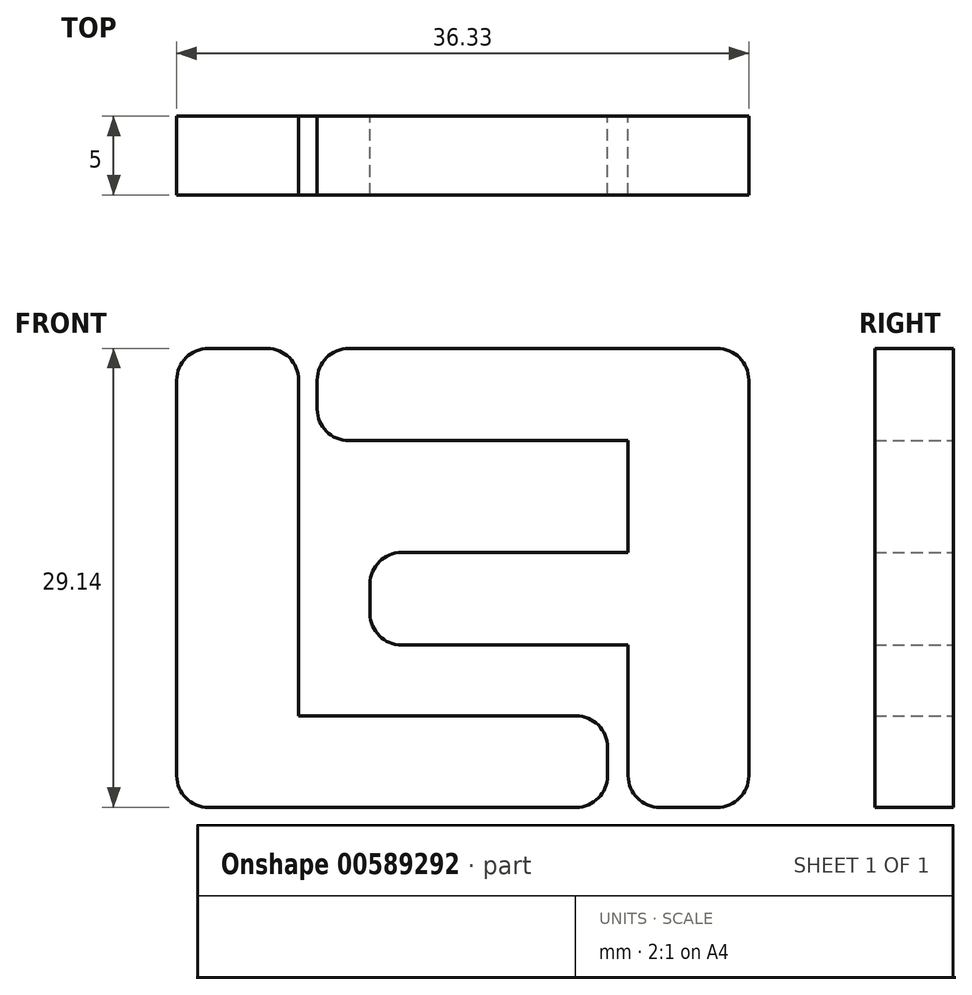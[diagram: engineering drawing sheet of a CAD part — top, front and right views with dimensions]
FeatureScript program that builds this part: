
annotation { "Feature Type Name" : "Feature", "Feature Type Description" : "" }
export const myFeature = defineFeature(function(context is Context, id is Id, definition is map)
    precondition{}
    {
        {
            var Q0;
            Q0=qCreatedBy(makeId("Front.planeOp"),FACE);
            var sketch = newSketch(context, id + "F0", { "sketchPlane" : qUnion([Q0])});
            skLineSegment(sketch, "E0", {"start": v(-17.2, 14.75) * mm, "end": v(-17.2, -14.4) * mm});
            skLineSegment(sketch, "E1", {"start": v(-17.2, -14.4) * mm, "end": v(10.15, -14.4) * mm});
            skLineSegment(sketch, "E2", {"start": v(10.15, -14.4) * mm, "end": v(10.15, -8.6) * mm});
            skLineSegment(sketch, "E3", {"start": v(10.15, -8.6) * mm, "end": v(-9.47, -8.6) * mm});
            skLineSegment(sketch, "E4", {"start": v(-9.47, -8.6) * mm, "end": v(-9.47, 14.75) * mm});
            skLineSegment(sketch, "E5", {"start": v(-9.47, 14.75) * mm, "end": v(-17.2, 14.75) * mm});
            skLineSegment(sketch, "E6", {"start": v(-8.29, 14.75) * mm, "end": v(-8.29, 8.9) * mm});
            skLineSegment(sketch, "E7", {"start": v(-8.29, 8.9) * mm, "end": v(11.46, 8.9) * mm});
            skLineSegment(sketch, "E8", {"start": v(11.46, 8.9) * mm, "end": v(11.46, 1.8) * mm});
            skLineSegment(sketch, "E9", {"start": v(11.46, 1.8) * mm, "end": v(-4.93, 1.8) * mm});
            skLineSegment(sketch, "E10", {"start": v(-4.93, 1.8) * mm, "end": v(-4.93, -4.09) * mm});
            skLineSegment(sketch, "E11", {"start": v(-4.93, -4.09) * mm, "end": v(11.46, -4.09) * mm});
            skLineSegment(sketch, "E12", {"start": v(11.46, -4.09) * mm, "end": v(11.46, -14.4) * mm});
            skLineSegment(sketch, "E13", {"start": v(11.46, -14.4) * mm, "end": v(19.12, -14.4) * mm});
            skLineSegment(sketch, "E14", {"start": v(19.12, -14.4) * mm, "end": v(19.12, 14.75) * mm});
            skLineSegment(sketch, "E15", {"start": v(19.12, 14.75) * mm, "end": v(-8.29, 14.75) * mm});
            skSolve(sketch);
        }
        {
            var Q0;
            Q0 = qSketchRegion(id + "F0", true);
            extrude(context, id + "F1", {"entities" : qUnion([Q0]), "depth" : 5 * mm, "offsetDistance" : 25 * mm});
        }
        {
            var Q0;
            Q0=makeQuery(id+"F1.opExtrude","SWEPT_EDGE",EDGE,{"disambiguationData":[OSD([sQuery(id+"F0.wireOp",EDGE,"E0"),sQuery(id+"F0.wireOp",EDGE,"E5")])]});
            var Q1;
            Q1=makeQuery(id+"F1.opExtrude","SWEPT_EDGE",EDGE,{"disambiguationData":[OSD([sQuery(id+"F0.wireOp",EDGE,"E4"),sQuery(id+"F0.wireOp",EDGE,"E5")])]});
            var Q2;
            Q2=makeQuery(id+"F1.opExtrude","SWEPT_EDGE",EDGE,{"disambiguationData":[OSD([sQuery(id+"F0.wireOp",EDGE,"E0"),sQuery(id+"F0.wireOp",EDGE,"E1")])]});
            var Q3;
            Q3=makeQuery(id+"F1.opExtrude","SWEPT_EDGE",EDGE,{"disambiguationData":[OSD([sQuery(id+"F0.wireOp",EDGE,"E1"),sQuery(id+"F0.wireOp",EDGE,"E2")])]});
            var Q4;
            Q4=makeQuery(id+"F1.opExtrude","SWEPT_EDGE",EDGE,{"disambiguationData":[OSD([sQuery(id+"F0.wireOp",EDGE,"E2"),sQuery(id+"F0.wireOp",EDGE,"E3")])]});
            var Q5;
            Q5=makeQuery(id+"F1.opExtrude","SWEPT_EDGE",EDGE,{"disambiguationData":[OSD([sQuery(id+"F0.wireOp",EDGE,"E12"),sQuery(id+"F0.wireOp",EDGE,"E13")])]});
            var Q6;
            Q6=makeQuery(id+"F1.opExtrude","SWEPT_EDGE",EDGE,{"disambiguationData":[OSD([sQuery(id+"F0.wireOp",EDGE,"E13"),sQuery(id+"F0.wireOp",EDGE,"E14")])]});
            var Q7;
            Q7=makeQuery(id+"F1.opExtrude","SWEPT_EDGE",EDGE,{"disambiguationData":[OSD([sQuery(id+"F0.wireOp",EDGE,"E14"),sQuery(id+"F0.wireOp",EDGE,"E15")])]});
            var Q8;
            Q8=makeQuery(id+"F1.opExtrude","SWEPT_EDGE",EDGE,{"disambiguationData":[OSD([sQuery(id+"F0.wireOp",EDGE,"E10"),sQuery(id+"F0.wireOp",EDGE,"E11")])]});
            var Q9;
            Q9=makeQuery(id+"F1.opExtrude","SWEPT_EDGE",EDGE,{"disambiguationData":[OSD([sQuery(id+"F0.wireOp",EDGE,"E9"),sQuery(id+"F0.wireOp",EDGE,"E10")])]});
            var Q10;
            Q10=makeQuery(id+"F1.opExtrude","SWEPT_EDGE",EDGE,{"disambiguationData":[OSD([sQuery(id+"F0.wireOp",EDGE,"E6"),sQuery(id+"F0.wireOp",EDGE,"E7")])]});
            var Q11;
            Q11=makeQuery(id+"F1.opExtrude","SWEPT_EDGE",EDGE,{"disambiguationData":[OSD([sQuery(id+"F0.wireOp",EDGE,"E6"),sQuery(id+"F0.wireOp",EDGE,"E15")])]});
            fillet(context, id + "F2", {"entities" : qUnion([Q0, Q1, Q2, Q3, Q4, Q5, Q6, Q7, Q8, Q9, Q10, Q11]), "radius" : 2 * mm, "tangentPropagation" : true, "allowEdgeOverflow" : false});
        }
    });
